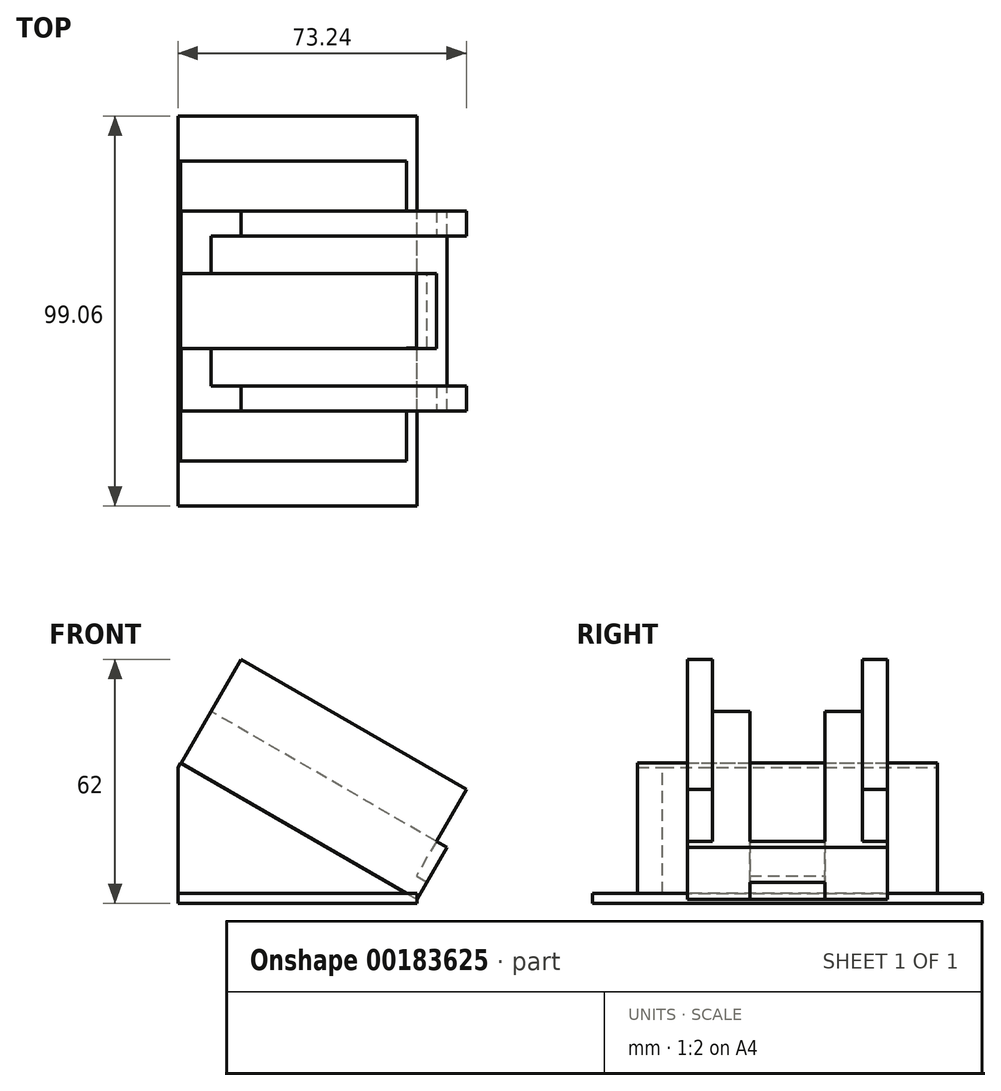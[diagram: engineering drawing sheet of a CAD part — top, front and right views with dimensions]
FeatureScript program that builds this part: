
annotation { "Feature Type Name" : "Feature", "Feature Type Description" : "" }
export const myFeature = defineFeature(function(context is Context, id is Id, definition is map)
    precondition{}
    {
        {
            var Q0;
            Q0=qCreatedBy(makeId("Front.planeOp"),FACE);
            var sketch = newSketch(context, id + "F0", { "sketchPlane" : qUnion([Q0])});
            skLineSegment(sketch, "E0", {"start": v(0, 0) * mm, "end": v(-60.11, 34.7) * mm});
            skLineSegment(sketch, "E1", {"start": v(-60.11, 34.7) * mm, "end": v(-60.75, 33.6) * mm});
            skLineSegment(sketch, "E2", {"start": v(-60.75, 33.6) * mm, "end": v(-0.8, -1) * mm});
            skLineSegment(sketch, "E3", {"start": v(-0.8, -1) * mm, "end": v(0, 0) * mm});
            skSolve(sketch);
        }
        {
            var Q0;
            Q0 = qSketchRegion(id + "F0", true);
            extrude(context, id + "F1", {"entities" : qUnion([Q0]), "endBound" : BoundingType.SYMMETRIC, "depth" : 76.2 * mm});
        }
        {
            var Q0;
            Q0=makeQuery(id+"F1.opExtrude","SWEPT_FACE",FACE,{"disambiguationData":[OSD([sQuery(id+"F0.wireOp",EDGE,"E0")])]});
            var sketch = newSketch(context, id + "F2", { "sketchPlane" : qUnion([Q0])});
            skLineSegment(sketch, "E4.bottom", {"start": v(-3.18, 25.4) * mm, "end": v(0, 25.4) * mm});
            skLineSegment(sketch, "E4.top", {"start": v(-3.17, -25.4) * mm, "end": v(0, -25.4) * mm});
            skLineSegment(sketch, "E4.left", {"start": v(-3.18, 25.4) * mm, "end": v(-3.18, -25.4) * mm});
            skLineSegment(sketch, "E4.right", {"start": v(0, 25.4) * mm, "end": v(0, -25.4) * mm});
            skLineSegment(sketch, "E5.bottom", {"start": v(-3.18, 9.53) * mm, "end": v(-69.22, 9.53) * mm});
            skLineSegment(sketch, "E5.top", {"start": v(-3.17, -9.52) * mm, "end": v(-69.22, -9.53) * mm});
            skLineSegment(sketch, "E5.left", {"start": v(-3.18, 9.53) * mm, "end": v(-3.18, -9.52) * mm});
            skLineSegment(sketch, "E5.right", {"start": v(-69.22, 9.53) * mm, "end": v(-69.22, -9.53) * mm});
            skLineSegment(sketch, "E6.bottom", {"start": v(-3.18, 19.05) * mm, "end": v(-69.22, 19.05) * mm});
            skLineSegment(sketch, "E6.top", {"start": v(-3.17, -19.05) * mm, "end": v(-69.22, -19.05) * mm});
            skLineSegment(sketch, "E6.left", {"start": v(-3.18, 19.05) * mm, "end": v(-3.18, -19.05) * mm});
            skLineSegment(sketch, "E6.right", {"start": v(-69.22, 19.05) * mm, "end": v(-69.22, -19.05) * mm});
            skLineSegment(sketch, "E7.bottom", {"start": v(-3.18, 25.4) * mm, "end": v(-69.22, 25.4) * mm});
            skLineSegment(sketch, "E7.top", {"start": v(-3.17, -25.4) * mm, "end": v(-69.21, -25.4) * mm});
            skLineSegment(sketch, "E7.right", {"start": v(-69.22, 25.4) * mm, "end": v(-69.21, -25.4) * mm});
            skSolve(sketch);
        }
        {
            var Q0;
            {var subQ0=sQuery(id+"F2.wireOp",EDGE,"E5.top");Q0=makeQuery(id+"F2.imprint","IMPRINT",FACE,{"disambiguationData":[TD([[makeQuery(id+"F2.imprint","IMPRINT",EDGE,{"derivedFrom":subQ0}),1.0]])]});}
            var Q1;
            {var subQ0=sQuery(id+"F2.wireOp",EDGE,"E5.bottom");Q1=makeQuery(id+"F2.imprint","IMPRINT",FACE,{"disambiguationData":[TD([[makeQuery(id+"F2.imprint","IMPRINT",EDGE,{"derivedFrom":subQ0}),-1.0]])]});}
            extrude(context, id + "F3", {"entities" : qUnion([Q0, Q1]), "operationType" : NewBodyOperationType.ADD, "depth" : 15.24 * mm});
        }
        {
            var Q0;
            {var subQ0=sQuery(id+"F2.wireOp",EDGE,"E6.top");Q0=makeQuery(id+"F2.imprint","IMPRINT",FACE,{"disambiguationData":[TD([[makeQuery(id+"F2.imprint","IMPRINT",EDGE,{"derivedFrom":subQ0}),1.0]])]});}
            var Q1;
            {var subQ0=sQuery(id+"F2.wireOp",EDGE,"E6.bottom");Q1=makeQuery(id+"F2.imprint","IMPRINT",FACE,{"disambiguationData":[TD([[makeQuery(id+"F2.imprint","IMPRINT",EDGE,{"derivedFrom":subQ0}),-1.0]])]});}
            extrude(context, id + "F4", {"entities" : qUnion([Q0, Q1]), "operationType" : NewBodyOperationType.ADD, "depth" : 30.48 * mm});
        }
        {
            var Q0;
            {var subQ4=sQuery(id+"F2.wireOp",EDGE,"E4.bottom");Q0=makeQuery(id+"F2.imprint","IMPRINT",FACE,{"disambiguationData":[TD([[makeQuery(id+"F2.imprint","IMPRINT",EDGE,{"derivedFrom":subQ4}),-1.0]])]});}
            extrude(context, id + "F5", {"entities" : qUnion([Q0]), "operationType" : NewBodyOperationType.ADD, "depth" : 15.24 * mm});
        }
        {
            var Q0;
            Q0=makeQuery(id+"F5.opExtrude","SWEPT_FACE",FACE,{"disambiguationData":[OSD([sQuery(id+"F2.wireOp",EDGE,"E4.right")])]});
            var sketch = newSketch(context, id + "F6", { "sketchPlane" : qUnion([Q0])});
            skLineSegment(sketch, "E8.bottom", {"start": v(-9.53, 5.08) * mm, "end": v(9.52, 5.08) * mm});
            skLineSegment(sketch, "E8.top", {"start": v(-9.53, 0) * mm, "end": v(9.52, 0) * mm});
            skLineSegment(sketch, "E8.left", {"start": v(-9.53, 5.08) * mm, "end": v(-9.53, 0) * mm});
            skLineSegment(sketch, "E8.right", {"start": v(9.52, 5.08) * mm, "end": v(9.52, 0) * mm});
            skSolve(sketch);
        }
        {
            var Q0;
            Q0 = qSketchRegion(id + "F6", true);
            extrude(context, id + "F7", {"entities" : qUnion([Q0]), "operationType" : NewBodyOperationType.REMOVE, "oppositeDirection" : true, "depth" : 3.17 * mm});
        }
        {
            var Q0;
            Q0=makeQuery(id+"F1.opExtrude","CAP_FACE",FACE,{"disambiguationData":[OSD([sQuery(id+"F0.wireOp",EDGE,"E0"),sQuery(id+"F0.wireOp",EDGE,"E1"),sQuery(id+"F0.wireOp",EDGE,"E2"),sQuery(id+"F0.wireOp",EDGE,"E3")])],"isStart":false});
            var sketch = newSketch(context, id + "F8", { "sketchPlane" : qUnion([Q0])});
            skLineSegment(sketch, "E9", {"start": v(-0.8, -1) * mm, "end": v(-60.75, -1) * mm});
            skLineSegment(sketch, "E10", {"start": v(-60.75, -1) * mm, "end": v(-60.75, 33.6) * mm});
            skLineSegment(sketch, "E11", {"start": v(-60.75, 33.6) * mm, "end": v(-0.8, -1) * mm});
            skSolve(sketch);
        }
        {
            var Q0;
            Q0 = qSketchRegion(id + "F8", true);
            extrude(context, id + "F9", {"entities" : qUnion([Q0]), "operationType" : NewBodyOperationType.ADD, "oppositeDirection" : true, "depth" : 6.35 * mm});
        }
        {
            var Q0;
            Q0=makeQuery(id+"F1.opExtrude","CAP_FACE",FACE,{"disambiguationData":[OSD([sQuery(id+"F0.wireOp",EDGE,"E0"),sQuery(id+"F0.wireOp",EDGE,"E1"),sQuery(id+"F0.wireOp",EDGE,"E2"),sQuery(id+"F0.wireOp",EDGE,"E3")])],"isStart":true});
            var sketch = newSketch(context, id + "F10", { "sketchPlane" : qUnion([Q0])});
            skLineSegment(sketch, "E12", {"start": v(0.8, -1) * mm, "end": v(60.7, -1) * mm});
            skLineSegment(sketch, "E13", {"start": v(60.7, -1) * mm, "end": v(60.75, 33.6) * mm});
            skLineSegment(sketch, "E14", {"start": v(60.75, 33.6) * mm, "end": v(0.8, -1) * mm});
            skSolve(sketch);
        }
        {
            var Q0;
            Q0 = qSketchRegion(id + "F10", true);
            extrude(context, id + "F11", {"entities" : qUnion([Q0]), "operationType" : NewBodyOperationType.ADD, "oppositeDirection" : true, "depth" : 3.17 * mm});
        }
        {
            var Q0;
            Q0=makeQuery(id+"F9.opExtrude","SWEPT_FACE",FACE,{"disambiguationData":[OSD([sQuery(id+"F8.wireOp",EDGE,"E9")])]});
            var sketch = newSketch(context, id + "F12", { "sketchPlane" : qUnion([Q0])});
            skLineSegment(sketch, "E15.bottom", {"start": v(-60.75, 49.53) * mm, "end": v(0, 49.53) * mm});
            skLineSegment(sketch, "E15.top", {"start": v(-60.75, -49.53) * mm, "end": v(0, -49.53) * mm});
            skLineSegment(sketch, "E15.left", {"start": v(-60.75, 49.53) * mm, "end": v(-60.75, -49.53) * mm});
            skLineSegment(sketch, "E15.right", {"start": v(0, 49.53) * mm, "end": v(0, -49.53) * mm});
            skLineSegment(sketch, "E16.left", {"start": v(0, 9.53) * mm, "end": v(0, -9.52) * mm});
            skSolve(sketch);
        }
        {
            var Q0;
            {var subQ2=sQuery(id+"F12.wireOp",EDGE,"E15.bottom");Q0=makeQuery(id+"F12.imprint","IMPRINT",FACE,{"disambiguationData":[TD([[makeQuery(id+"F12.imprint","IMPRINT",EDGE,{"derivedFrom":subQ2}),-1.0]])]});}
            extrude(context, id + "F13", {"entities" : qUnion([Q0]), "operationType" : NewBodyOperationType.ADD, "oppositeDirection" : true, "depth" : 2.54 * mm});
        }
        {
            var Q0;
            {var subQ0=sQuery(id+"F2.wireOp",EDGE,"E5.bottom");Q0=makeQuery(id+"F2.imprint","IMPRINT",FACE,{"disambiguationData":[TD([[makeQuery(id+"F2.imprint","IMPRINT",EDGE,{"derivedFrom":subQ0}),1.0]])]});}
            var sketch = newSketch(context, id + "F14", { "sketchPlane" : qUnion([Q0])});
            skLineSegment(sketch, "E17.bottom", {"start": v(-8.4, -9.45) * mm, "end": v(3.82, -9.45) * mm});
            skLineSegment(sketch, "E17.top", {"start": v(-8.4, 9.53) * mm, "end": v(3.82, 9.53) * mm});
            skLineSegment(sketch, "E17.left", {"start": v(-8.4, -9.45) * mm, "end": v(-8.4, 9.53) * mm});
            skLineSegment(sketch, "E17.right", {"start": v(3.82, -9.45) * mm, "end": v(3.82, 9.53) * mm});
            skSolve(sketch);
        }
        {
            var Q0;
            Q0 = qSketchRegion(id + "F14", true);
            extrude(context, id + "F15", {"entities" : qUnion([Q0]), "operationType" : NewBodyOperationType.REMOVE, "depth" : 2.54 * mm});
        }
        {
            var Q0;
            {var subQ0=sQuery(id+"F12.wireOp",EDGE,"E15.left");var subQ1=sQuery(id+"F8.wireOp",EDGE,"E9");var subQ3=sQuery(id+"F12.wireOp",EDGE,"E15.top");var subQ5=sQuery(id+"F12.wireOp",EDGE,"E15.bottom");var subQ7=sQuery(id+"F8.wireOp",EDGE,"E11");var subQ8=sQuery(id+"F0.wireOp",EDGE,"E3");var subQ9=sQuery(id+"F0.wireOp",EDGE,"E2");var subQ11=sQuery(id+"F12.wireOp",EDGE,"E16.left");var subQ12=sQuery(id+"F12.wireOp",EDGE,"E15.right");Q0=makeQuery(id+"F13.boolean.opBoolean","SPLIT",FACE,{"disambiguationData":[TD([makeQuery(id+"F4.opExtrude","SWEPT_FACE",FACE,{"disambiguationData":[OSD([sQuery(id+"F2.wireOp",EDGE,"E7.top")])]})])],"derivedFrom":makeQuery(id+"F13.opExtrude","CAP_FACE",FACE,{"disambiguationData":[OSD([subQ9,subQ8,subQ1,subQ7,subQ5,subQ3,subQ0,subQ12,subQ11])],"isStart":false})});}
            var sketch = newSketch(context, id + "F16", { "sketchPlane" : qUnion([Q0])});
            skLineSegment(sketch, "E18.bottom", {"start": v(-2.67, -31.75) * mm, "end": v(-0.8, -31.75) * mm});
            skLineSegment(sketch, "E18.top", {"start": v(-2.67, -38.1) * mm, "end": v(-0.8, -38.1) * mm});
            skLineSegment(sketch, "E18.left", {"start": v(-2.67, -31.75) * mm, "end": v(-2.67, -38.1) * mm});
            skLineSegment(sketch, "E18.right", {"start": v(-0.8, -31.75) * mm, "end": v(-0.8, -38.1) * mm});
            skSolve(sketch);
        }
        {
            var Q0;
            Q0 = qSketchRegion(id + "F16", true);
            extrude(context, id + "F17", {"entities" : qUnion([Q0]), "operationType" : NewBodyOperationType.ADD, "oppositeDirection" : true, "depth" : 2.54 * mm});
        }
        {
            var Q0;
            Q0=makeQuery(id+"F11.opExtrude","CAP_FACE",FACE,{"disambiguationData":[OSD([sQuery(id+"F10.wireOp",EDGE,"E12"),sQuery(id+"F10.wireOp",EDGE,"E13"),sQuery(id+"F10.wireOp",EDGE,"E14")])],"isStart":false});
            var sketch = newSketch(context, id + "F18", { "sketchPlane" : qUnion([Q0])});
            skLineSegment(sketch, "E19", {"start": v(-5.2, 1.54) * mm, "end": v(-60.75, 33.6) * mm});
            skLineSegment(sketch, "E20", {"start": v(-60.75, 33.6) * mm, "end": v(-60.7, 1.54) * mm});
            skLineSegment(sketch, "E21", {"start": v(-60.7, 1.54) * mm, "end": v(-5.2, 1.54) * mm});
            skSolve(sketch);
        }
        {
            var Q0;
            Q0 = qSketchRegion(id + "F18", true);
            extrude(context, id + "F19", {"entities" : qUnion([Q0]), "operationType" : NewBodyOperationType.ADD, "depth" : 66.67 * mm});
        }
    });
